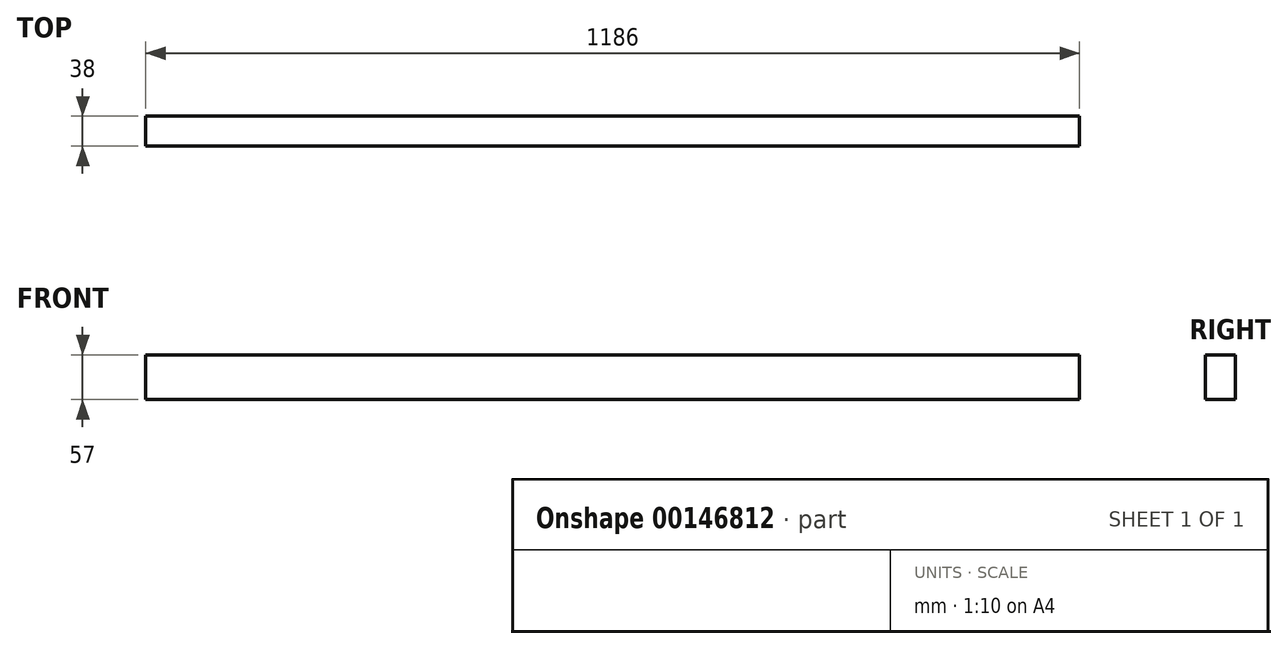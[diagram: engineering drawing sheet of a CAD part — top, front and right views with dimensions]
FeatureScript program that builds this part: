
annotation { "Feature Type Name" : "Feature", "Feature Type Description" : "" }
export const myFeature = defineFeature(function(context is Context, id is Id, definition is map)
    precondition{}
    {
        {
            var Q0;
            Q0=qCreatedBy(makeId("Top.planeOp"),FACE);
            var sketch = newSketch(context, id + "F0", { "sketchPlane" : qUnion([Q0])});
            skLineSegment(sketch, "E0.bottom", {"start": v(0, 0) * mm, "end": v(1186, 0) * mm});
            skLineSegment(sketch, "E0.top", {"start": v(0, 38) * mm, "end": v(1186, 38) * mm});
            skLineSegment(sketch, "E0.left", {"start": v(0, 0) * mm, "end": v(0, 38) * mm});
            skLineSegment(sketch, "E0.right", {"start": v(1186, 0) * mm, "end": v(1186, 38) * mm});
            skSolve(sketch);
        }
        {
            var Q0;
            Q0 = qSketchRegion(id + "F0", true);
            extrude(context, id + "F1", {"entities" : qUnion([Q0]), "depth" : 57 * mm});
        }
    });
